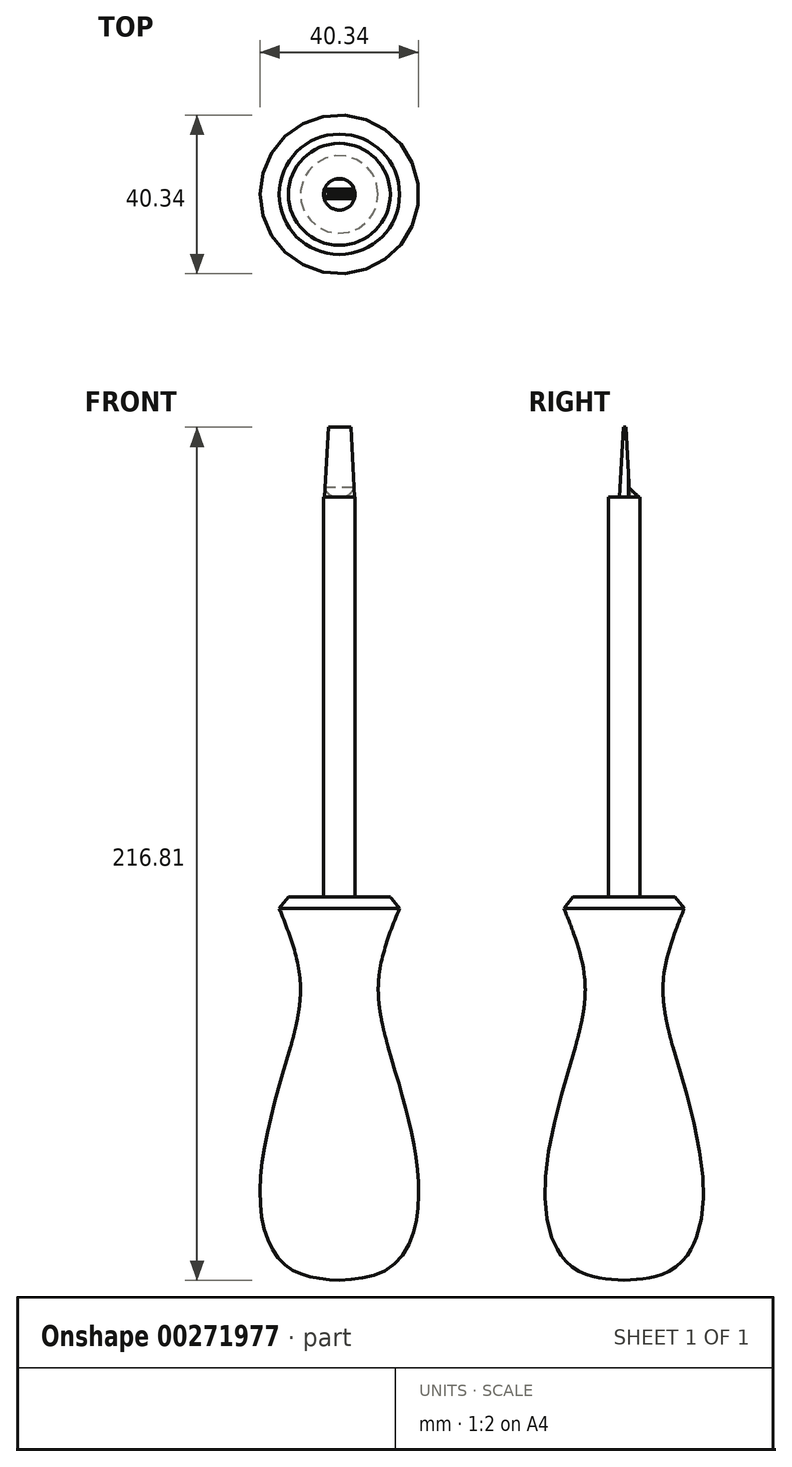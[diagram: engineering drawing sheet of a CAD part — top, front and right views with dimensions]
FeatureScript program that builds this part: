
annotation { "Feature Type Name" : "Feature", "Feature Type Description" : "" }
export const myFeature = defineFeature(function(context is Context, id is Id, definition is map)
    precondition{}
    {
        {
            var Q0;
            Q0=qCreatedBy(makeId("Front.planeOp"),FACE);
            var sketch = newSketch(context, id + "F0", { "sketchPlane" : qUnion([Q0])});
            skPoint(sketch, "E0.start.orphan", {"position": v(0, 54.36) * mm});
            skLineSegment(sketch, "E1", {"start": v(0, 54.36) * mm, "end": v(0, -68) * mm});
            skLineSegment(sketch, "E2", {"start": v(0, 29.42) * mm, "end": v(-12.94, 29.42) * mm});
            skLineSegment(sketch, "E3", {"start": v(-12.94, 29.42) * mm, "end": v(-15.3, 26.6) * mm});
            skFitSpline(sketch, "E4", {"points": [v(-15.3, 26.6) * mm, v(-9.88, 6.59) * mm, v(-15.3, -18.6) * mm, v(-20, -49.65) * mm, v(-12.94, -64.71) * mm, v(0, -68) * mm], "startDerivative": vector(39.82, -99) * mm, "endDerivative": vector(88.7, -7.19) * mm});
            skArc(sketch, "E5", {"start": v(-10.02, 8.88) * mm, "mid": v(-12.18, 6.54) * mm, "end": v(-9.92, 4.3) * mm});
            skArc(sketch, "E6", {"start": v(-10.08, 2.27) * mm, "mid": v(-12.65, 0.36) * mm, "end": v(-10.8, -2.25) * mm});
            skArc(sketch, "E7", {"start": v(-11.13, -3.77) * mm, "mid": v(-14.16, -5.58) * mm, "end": v(-12.38, -8.63) * mm});
            skSolve(sketch);
        }
        {
            var Q0;
            {var subQ2=sQuery(id+"F0.wireOp",EDGE,"E2");Q0=makeQuery(id+"F0.imprint","IMPRINT",FACE,{"disambiguationData":[TD([[makeQuery(id+"F0.imprint","IMPRINT",EDGE,{"derivedFrom":subQ2}),1.0]])]});}
            var Q1;
            Q1=sQuery(id+"F0.wireOp",EDGE,"E1");
            revolve(context, id + "F1", {"entities" : qUnion([Q0]), "axis" : qUnion([Q1]), "revolveType" : RevolveType.FULL});
        }
        {
            var Q0;
            Q0=makeQuery(id+"F1.opRevolve","SWEPT_FACE",FACE,{"disambiguationData":[OSD([sQuery(id+"F0.wireOp",EDGE,"E2")])]});
            var sketch = newSketch(context, id + "F2", { "sketchPlane" : qUnion([Q0])});
            skCircle(sketch, "E8", {"center": v(0, 0) * mm, "radius": 4 * mm});
            skSolve(sketch);
        }
        {
            var Q0;
            Q0=makeQuery(id+"F2.imprint","IMPRINT",FACE,{"disambiguationData":[TD([[makeQuery(id+"F2.imprint","IMPRINT",EDGE,{"derivedFrom":sQuery(id+"F2.wireOp",EDGE,"E8")}),1.0]])]});
            extrude(context, id + "F3", {"entities" : qUnion([Q0]), "operationType" : NewBodyOperationType.ADD, "depth" : 101.6 * mm});
        }
        {
            var Q0;
            Q0=makeQuery(id+"F3.opExtrude","CAP_FACE",FACE,{"disambiguationData":[OSD([sQuery(id+"F2.wireOp",EDGE,"E8")])],"isStart":false});
            var sketch = newSketch(context, id + "F4", { "sketchPlane" : qUnion([Q0])});
            skLineSegment(sketch, "E9.bottom", {"start": v(-3.74, 1.41) * mm, "end": v(3.83, 1.41) * mm});
            skLineSegment(sketch, "E9.top", {"start": v(-3.74, -1.14) * mm, "end": v(3.83, -1.14) * mm});
            skLineSegment(sketch, "E9.left", {"start": v(-3.74, 1.41) * mm, "end": v(-3.74, -1.14) * mm});
            skLineSegment(sketch, "E9.right", {"start": v(3.83, 1.41) * mm, "end": v(3.83, -1.14) * mm});
            skSolve(sketch);
        }
        {
            var Q0;
            {var subQ1=sQuery(id+"F4.wireOp",EDGE,"E9.top");Q0=makeQuery(id+"F4.imprint","IMPRINT",FACE,{"disambiguationData":[TD([[makeQuery(id+"F4.imprint","IMPRINT",EDGE,{"derivedFrom":subQ1}),1.0]])]});}
            extrude(context, id + "F5", {"entities" : qUnion([Q0]), "operationType" : NewBodyOperationType.ADD, "depth" : 17.78 * mm, "hasDraft" : true, "draftAngle" : 3 * degree, "draftPullDirection" : true});
        }
        {
            var Q0;
            Q0=makeQuery(id+"F5.opExtrude","CAP_EDGE",EDGE,{"disambiguationData":[OSD([sQuery(id+"F4.wireOp",EDGE,"E9.top")])],"isStart":true});
            var Q1;
            Q1=makeQuery(id+"F5.opExtrude","CAP_EDGE",EDGE,{"disambiguationData":[OSD([sQuery(id+"F4.wireOp",EDGE,"E9.bottom")])],"isStart":true});
            chamfer(context, id + "F6", {"entities" : qUnion([Q0, Q1]), "width" : 2.54 * mm, "tangentPropagation" : true});
        }
    });
